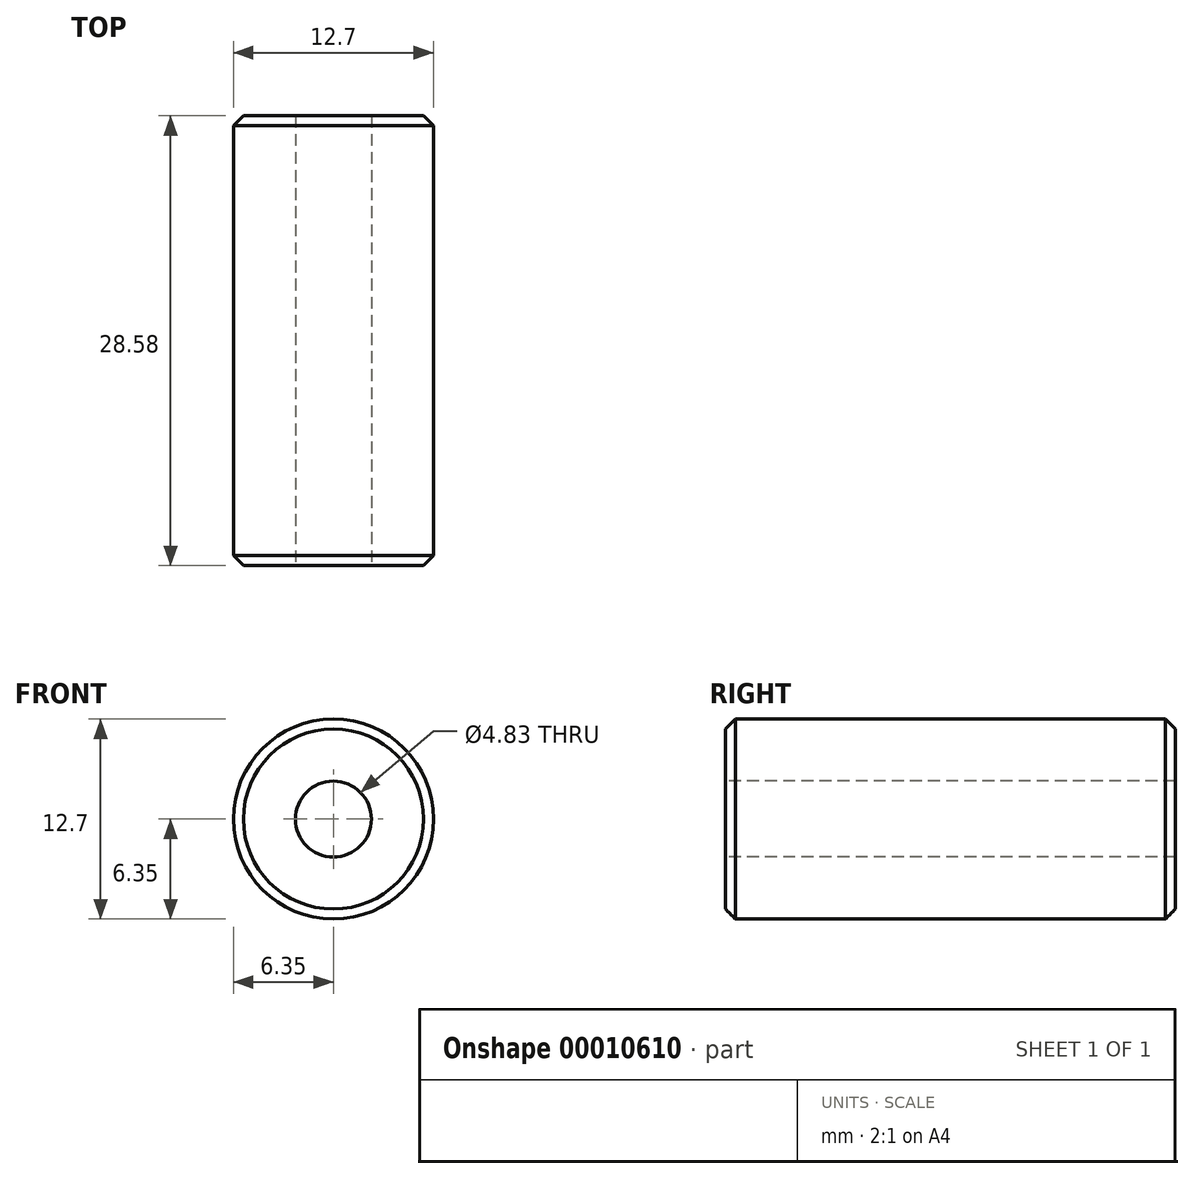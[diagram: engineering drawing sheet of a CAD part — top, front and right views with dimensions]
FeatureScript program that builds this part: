
annotation { "Feature Type Name" : "Feature", "Feature Type Description" : "" }
export const myFeature = defineFeature(function(context is Context, id is Id, definition is map)
    precondition{}
    {
        {
            var Q0;
            Q0=qCreatedBy(makeId("Front.planeOp"),FACE);
            var sketch = newSketch(context, id + "F0", { "sketchPlane" : qUnion([Q0])});
            skCircle(sketch, "E0", {"center": v(0, 0) * mm, "radius": 6.35 * mm});
            skCircle(sketch, "E1", {"center": v(0, 0) * mm, "radius": 2.41 * mm});
            skSolve(sketch);
        }
        {
            var Q0;
            Q0=qSketchRegion(id+"F0",true);
            extrude(context, id + "F1", {"entities" : qUnion([Q0]), "oppositeDirection" : true, "depth" : 28.57 * mm});
        }
        {
            var Q0;
            Q0=makeQuery(id+"F1.opExtrude","CAP_EDGE",EDGE,{"disambiguationData":[OSD([sQuery(id+"F0.wireOp",EDGE,"E0")])],"isStart":true});
            var Q1;
            Q1=makeQuery(id+"F1.opExtrude","CAP_EDGE",EDGE,{"disambiguationData":[OSD([sQuery(id+"F0.wireOp",EDGE,"E0")])],"isStart":false});
            chamfer(context, id + "F2", {"entities" : qUnion([Q0, Q1]), "width" : 0.64 * mm, "tangentPropagation" : true});
        }
    });
